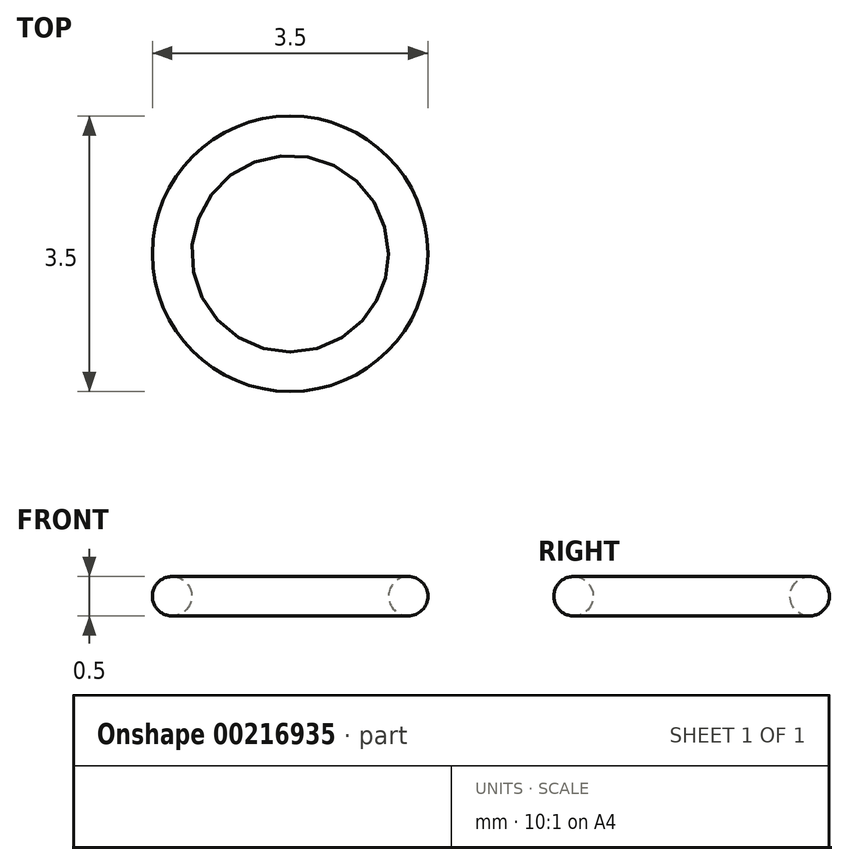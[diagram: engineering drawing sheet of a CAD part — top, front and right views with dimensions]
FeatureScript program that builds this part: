
annotation { "Feature Type Name" : "Feature", "Feature Type Description" : "" }
export const myFeature = defineFeature(function(context is Context, id is Id, definition is map)
    precondition{}
    {
        {
            var Q0;
            Q0=qCreatedBy(makeId("Top.planeOp"),FACE);
            var sketch = newSketch(context, id + "F0", { "sketchPlane" : qUnion([Q0])});
            skCircle(sketch, "E0", {"center": v(0, 0) * mm, "radius": 1.5 * mm});
            skSolve(sketch);
        }
        {
            var Q0;
            Q0=qCreatedBy(makeId("Front.planeOp"),FACE);
            var sketch = newSketch(context, id + "F1", { "sketchPlane" : qUnion([Q0])});
            skCircle(sketch, "E1", {"center": v(1.5, 0) * mm, "radius": 0.25 * mm});
            skSolve(sketch);
        }
        {
            var Q0;
            Q0 = qSketchRegion(id + "F1", true);
            var Q1;
            Q1 = qConstructionFilter(qBodyType(qCreatedBy(id + "F0" ,EDGE), BodyType.WIRE), ConstructionObject.NO);
            sweep(context, id + "F2", {"profiles" : qUnion([Q0]), "path" : qUnion([Q1])});
        }
    });
